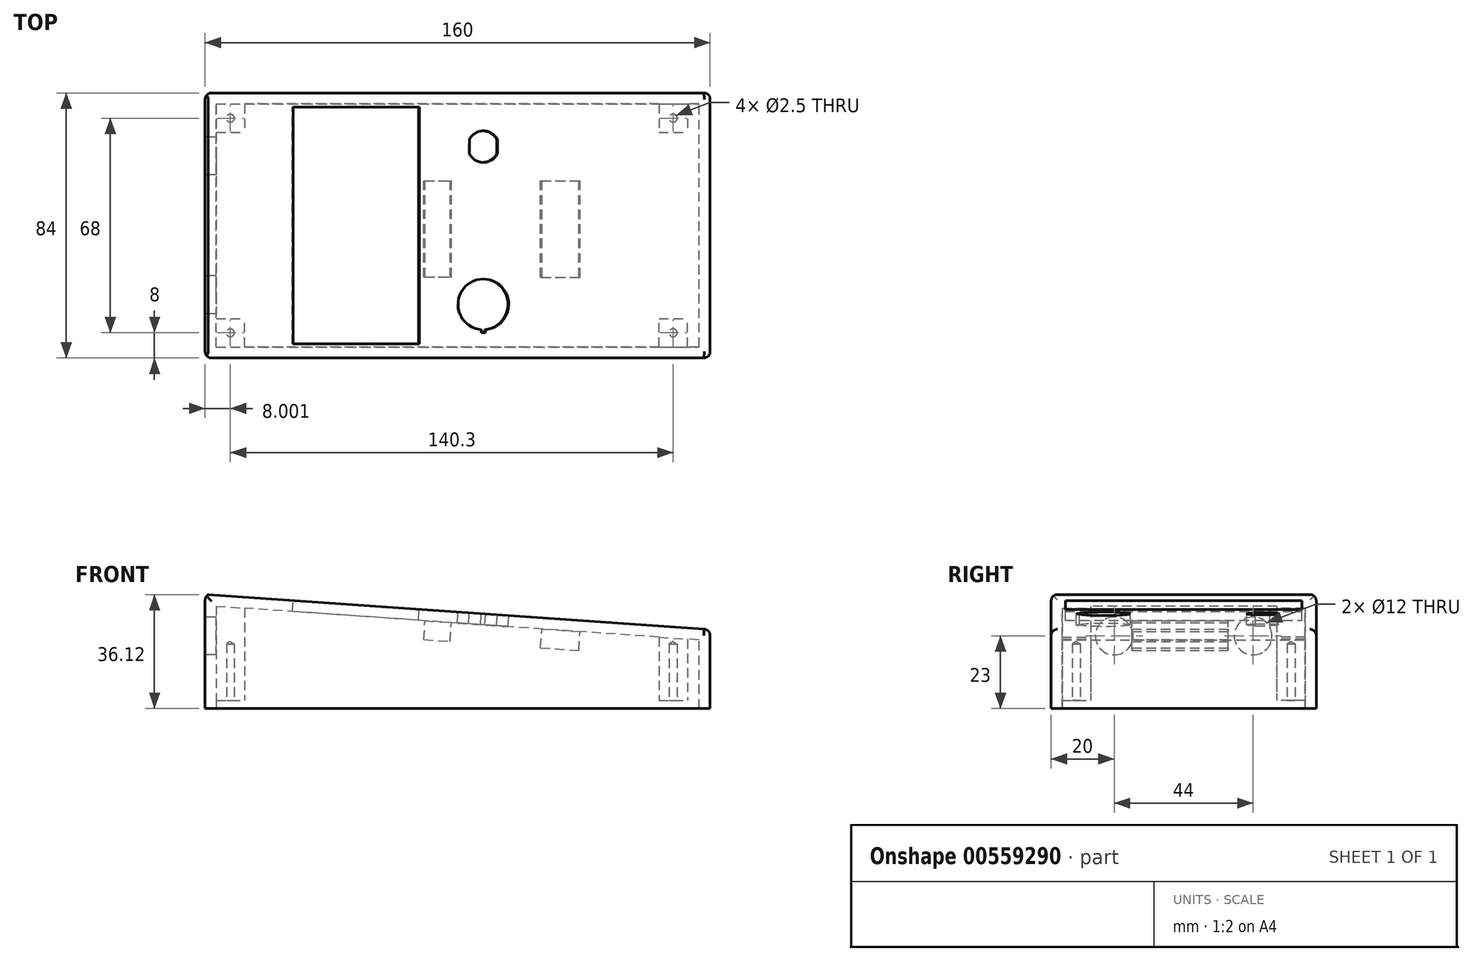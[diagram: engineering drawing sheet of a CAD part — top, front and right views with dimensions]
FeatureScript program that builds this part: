
annotation { "Feature Type Name" : "Feature", "Feature Type Description" : "" }
export const myFeature = defineFeature(function(context is Context, id is Id, definition is map)
    precondition{}
    {
        {
            var Q0;
            Q0=qCreatedBy(makeId("Front.planeOp"),FACE);
            var sketch = newSketch(context, id + "F0", { "sketchPlane" : qUnion([Q0])});
            skLineSegment(sketch, "E0", {"start": v(-94.59, 0) * mm, "end": v(103.68, 0) * mm, "construction": true});
            skLineSegment(sketch, "E1", {"start": v(0, 82.66) * mm, "end": v(0, -62.2) * mm, "construction": true});
            skLineSegment(sketch, "E2", {"start": v(-66.64, 0) * mm, "end": v(93.36, 0) * mm});
            skLineSegment(sketch, "E3", {"start": v(93.36, 0) * mm, "end": v(93.36, 25) * mm});
            skLineSegment(sketch, "E4", {"start": v(93.36, 25) * mm, "end": v(-65.64, 36.12) * mm});
            skLineSegment(sketch, "E5", {"start": v(-65.64, 36.12) * mm, "end": v(-66.64, 36.12) * mm});
            skLineSegment(sketch, "E6", {"start": v(-66.64, 36.12) * mm, "end": v(-66.64, 0) * mm});
            skLineSegment(sketch, "E7", {"start": v(93.36, 25) * mm, "end": v(-44.16, 25) * mm, "construction": true});
            skSolve(sketch);
        }
        {
            var Q0;
            Q0 = qSketchRegion(id + "F0", true);
            extrude(context, id + "F1", {"entities" : qUnion([Q0]), "endBound" : BoundingType.SYMMETRIC, "depth" : 84 * mm, "offsetDistance" : 25 * mm});
        }
        {
            var Q0;
            Q0=makeQuery(id+"F1.opExtrude","SWEPT_FACE",FACE,{"disambiguationData":[OSD([sQuery(id+"F0.wireOp",EDGE,"E2")])]});
            shell(context, id + "F2", {"entities" : qUnion([Q0]), "thickness" : 3.5 * mm});
        }
        {
            var Q0;
            Q0=makeQuery(id+"F1.opExtrude","SWEPT_FACE",FACE,{"disambiguationData":[OSD([sQuery(id+"F0.wireOp",EDGE,"E4")])]});
            var sketch = newSketch(context, id + "F3", { "sketchPlane" : qUnion([Q0])});
            skLineSegment(sketch, "E8", {"start": v(-77.74, 0) * mm, "end": v(107.26, 0) * mm, "construction": true});
            skLineSegment(sketch, "E9", {"start": v(-2.68, 70.27) * mm, "end": v(-2.68, -46.47) * mm, "construction": true});
            skLineSegment(sketch, "E10", {"start": v(31.39, 67.05) * mm, "end": v(31.39, -68) * mm, "construction": true});
            skLineSegment(sketch, "E11", {"start": v(19.39, -65.22) * mm, "end": v(19.39, 69.42) * mm, "construction": true});
            skLineSegment(sketch, "E12", {"start": v(9.3, -25) * mm, "end": v(38.07, -25) * mm, "construction": true});
            skLineSegment(sketch, "E13", {"start": v(15.02, 25) * mm, "end": v(38.07, 25) * mm, "construction": true});
            skLineSegment(sketch, "E14", {"start": v(-68, 65.02) * mm, "end": v(-68, -30.89) * mm, "construction": true});
            skLineSegment(sketch, "E15", {"start": v(-41, 65.02) * mm, "end": v(-41, -30.89) * mm, "construction": true});
            skLineSegment(sketch, "E16", {"start": v(-41, -30.89) * mm, "end": v(-42.3, -30.89) * mm, "construction": true});
            skLineSegment(sketch, "E17.bottom", {"start": v(-41, 37.5) * mm, "end": v(-1, 37.5) * mm});
            skLineSegment(sketch, "E17.top", {"start": v(-41, -37.5) * mm, "end": v(-1, -37.5) * mm});
            skLineSegment(sketch, "E17.left", {"start": v(-41, 37.5) * mm, "end": v(-41, -37.5) * mm});
            skLineSegment(sketch, "E17.right", {"start": v(-1, 37.5) * mm, "end": v(-1, -37.5) * mm});
            skLineSegment(sketch, "E18.MirrorCS", {"start": v(27.6, -25) * mm, "end": v(-1.18, -25) * mm, "construction": true});
            skArc(sketch, "E19", {"start": v(14.94, 22.72) * mm, "mid": v(19.39, 20) * mm, "end": v(23.84, 22.72) * mm});
            skLineSegment(sketch, "E20", {"start": v(14.94, 27.28) * mm, "end": v(14.94, 22.72) * mm});
            skLineSegment(sketch, "E21.MirrorCS", {"start": v(23.84, 27.28) * mm, "end": v(23.84, 22.72) * mm});
            skArc(sketch, "E22.trimOffspring", {"start": v(23.84, 27.28) * mm, "mid": v(19.39, 30) * mm, "end": v(14.94, 27.28) * mm});
            skArc(sketch, "E23", {"start": v(20.04, -33.02) * mm, "mid": v(19.39, -16.95) * mm, "end": v(18.74, -33.02) * mm});
            skLineSegment(sketch, "E24.top", {"start": v(18.74, -34.02) * mm, "end": v(20.04, -34.02) * mm});
            skLineSegment(sketch, "E24.left", {"start": v(18.74, -33.02) * mm, "end": v(18.74, -34.02) * mm});
            skLineSegment(sketch, "E24.right", {"start": v(20.04, -33.02) * mm, "end": v(20.04, -34.02) * mm});
            skSolve(sketch);
        }
        {
            var Q0;
            Q0=makeQuery(id+"F3.imprint","IMPRINT",FACE,{"disambiguationData":[TD([[makeQuery(id+"F3.imprint","IMPRINT",EDGE,{"derivedFrom":sQuery(id+"F3.wireOp",EDGE,"1abdff49-32a7-4e46-9834-f7d7c9bdcb830.MirrorCS")}),-1.0]])]});
            var Q1;
            Q1=makeQuery(id+"F3.imprint","IMPRINT",FACE,{"disambiguationData":[TD([[makeQuery(id+"F3.imprint","IMPRINT",EDGE,{"derivedFrom":sQuery(id+"F3.wireOp",EDGE,"Tb5Z7JnE-D9wR-4kkP-e9h7-nN8Eiio6d8Eo")}),1.0]])]});
            var Q2;
            Q2=makeQuery(id+"F3.imprint","IMPRINT",FACE,{"disambiguationData":[TD([[makeQuery(id+"F3.imprint","IMPRINT",EDGE,{"derivedFrom":sQuery(id+"F3.wireOp",EDGE,"E17.bottom")}),-1.0]])]});
            extrude(context, id + "F4", {"entities" : qUnion([Q0, Q1, Q2]), "operationType" : NewBodyOperationType.REMOVE, "oppositeDirection" : true, "depth" : 4 * mm, "offsetDistance" : 25 * mm});
        }
        {
            var Q0;
            Q0=makeQuery(id+"F1.opExtrude","SWEPT_FACE",FACE,{"disambiguationData":[OSD([sQuery(id+"F0.wireOp",EDGE,"E2")])]});
            cPlane(context, id + "F5", {"entities" : qUnion([Q0]), "cplaneType" : CPlaneType.OFFSET, "offset" : 0 * mm, "width" : 150 * mm, "height" : 150 * mm});
        }
        {
            var Q0;
            Q0=makeQuery(id+"F3.imprint","IMPRINT",FACE,{"disambiguationData":[TD([[makeQuery(id+"F3.imprint","IMPRINT",EDGE,{"derivedFrom":sQuery(id+"F3.wireOp",EDGE,"E19")}),1.0]])]});
            var Q1;
            Q1=makeQuery(id+"F3.imprint","IMPRINT",FACE,{"disambiguationData":[TD([[makeQuery(id+"F3.imprint","IMPRINT",EDGE,{"derivedFrom":sQuery(id+"F3.wireOp",EDGE,"E23")}),1.0]])]});
            extrude(context, id + "F6", {"entities" : qUnion([Q0, Q1]), "operationType" : NewBodyOperationType.REMOVE, "oppositeDirection" : true, "depth" : 5 * mm, "offsetDistance" : 25 * mm});
        }
        {
            var Q0;
            Q0=qCreatedBy(id+"F5.planeOp",FACE);
            cPlane(context, id + "F7", {"entities" : qUnion([Q0]), "cplaneType" : CPlaneType.OFFSET, "offset" : 2.5 * mm, "oppositeDirection" : true, "width" : 150 * mm, "height" : 150 * mm});
        }
        {
            var Q0;
            Q0=qCreatedBy(id+"F7.planeOp",FACE);
            var sketch = newSketch(context, id + "F8", { "sketchPlane" : qUnion([Q0])});
            skLineSegment(sketch, "E25", {"start": v(-103.66, 0) * mm, "end": v(127.76, 0) * mm, "construction": true});
            skLineSegment(sketch, "E26", {"start": v(0, 82.93) * mm, "end": v(0, -76.71) * mm, "construction": true});
            skLineSegment(sketch, "E27.bottom", {"start": v(-63.14, 38.5) * mm, "end": v(-54.14, 38.5) * mm});
            skLineSegment(sketch, "E27.top", {"start": v(-63.14, 29.5) * mm, "end": v(-54.14, 29.5) * mm});
            skLineSegment(sketch, "E27.left", {"start": v(-63.14, 38.5) * mm, "end": v(-63.14, 29.5) * mm});
            skLineSegment(sketch, "E27.right", {"start": v(-54.14, 38.5) * mm, "end": v(-54.14, 29.5) * mm});
            skLineSegment(sketch, "E28.bottom", {"start": v(77.16, 38.5) * mm, "end": v(86.16, 38.5) * mm});
            skLineSegment(sketch, "E28.top", {"start": v(77.16, 29.5) * mm, "end": v(86.16, 29.5) * mm});
            skLineSegment(sketch, "E28.left", {"start": v(77.16, 38.5) * mm, "end": v(77.16, 29.5) * mm});
            skLineSegment(sketch, "E28.right", {"start": v(86.16, 38.5) * mm, "end": v(86.16, 29.5) * mm});
            skLineSegment(sketch, "E29.MirrorCS", {"start": v(-63.14, -29.5) * mm, "end": v(-54.14, -29.5) * mm});
            skLineSegment(sketch, "E30.MirrorCS", {"start": v(-63.14, -38.5) * mm, "end": v(-54.14, -38.5) * mm});
            skLineSegment(sketch, "E31.MirrorCS", {"start": v(-63.14, -38.5) * mm, "end": v(-63.14, -29.5) * mm});
            skLineSegment(sketch, "E32.MirrorCS", {"start": v(-54.14, -38.5) * mm, "end": v(-54.14, -29.5) * mm});
            skLineSegment(sketch, "E33.MirrorCS", {"start": v(77.16, -38.5) * mm, "end": v(77.16, -29.5) * mm});
            skLineSegment(sketch, "E34.MirrorCS", {"start": v(77.16, -38.5) * mm, "end": v(86.16, -38.5) * mm});
            skLineSegment(sketch, "E35.MirrorCS", {"start": v(86.16, -38.5) * mm, "end": v(86.16, -29.5) * mm});
            skLineSegment(sketch, "E36.MirrorCS", {"start": v(77.16, -29.5) * mm, "end": v(86.16, -29.5) * mm});
            skLineSegment(sketch, "E37", {"start": v(-58.64, 39.07) * mm, "end": v(-58.64, 26.98) * mm, "construction": true});
            skLineSegment(sketch, "E38", {"start": v(-63.59, 34) * mm, "end": v(-52.8, 34) * mm, "construction": true});
            skPoint(sketch, "E38.startSnap0", {"position": v(-63.14, 34) * mm});
            skPoint(sketch, "E39", {"position": v(-58.64, 34) * mm});
            skPoint(sketch, "E40.MirrorP", {"position": v(-58.64, -34) * mm});
            skLineSegment(sketch, "E41", {"start": v(70.14, 34) * mm, "end": v(88.02, 34) * mm, "construction": true});
            skLineSegment(sketch, "E42", {"start": v(81.66, 26.58) * mm, "end": v(81.66, 42.04) * mm, "construction": true});
            skPoint(sketch, "E43", {"position": v(81.66, 34) * mm});
            skPoint(sketch, "E44.MirrorP", {"position": v(81.66, -34) * mm});
            skSolve(sketch);
        }
        {
            var Q0;
            Q0=makeQuery(id+"F8.imprint","IMPRINT",FACE,{"disambiguationData":[TD([[makeQuery(id+"F8.imprint","IMPRINT",EDGE,{"derivedFrom":sQuery(id+"F8.wireOp",EDGE,"E28.bottom")}),-1.0]])]});
            var Q1;
            Q1=makeQuery(id+"F8.imprint","IMPRINT",FACE,{"disambiguationData":[TD([[makeQuery(id+"F8.imprint","IMPRINT",EDGE,{"derivedFrom":sQuery(id+"F8.wireOp",EDGE,"E33.MirrorCS")}),-1.0]])]});
            extrude(context, id + "F9", {"entities" : qUnion([Q0, Q1]), "operationType" : NewBodyOperationType.ADD, "oppositeDirection" : true, "depth" : 20.5 * mm, "offsetDistance" : 25 * mm});
        }
        {
            var Q0;
            Q0=makeQuery(id+"F8.imprint","IMPRINT",FACE,{"disambiguationData":[TD([[makeQuery(id+"F8.imprint","IMPRINT",EDGE,{"derivedFrom":sQuery(id+"F8.wireOp",EDGE,"E29.MirrorCS")}),-1.0]])]});
            var Q1;
            Q1=makeQuery(id+"F8.imprint","IMPRINT",FACE,{"disambiguationData":[TD([[makeQuery(id+"F8.imprint","IMPRINT",EDGE,{"derivedFrom":sQuery(id+"F8.wireOp",EDGE,"E27.bottom")}),-1.0]])]});
            extrude(context, id + "F10", {"entities" : qUnion([Q0, Q1]), "operationType" : NewBodyOperationType.ADD, "oppositeDirection" : true, "depth" : 32 * mm, "offsetDistance" : 25 * mm});
        }
        {
            var Q0;
            Q0=makeQuery(id+"F1.opExtrude","SWEPT_FACE",FACE,{"disambiguationData":[OSD([sQuery(id+"F0.wireOp",EDGE,"E6")])]});
            cPlane(context, id + "F11", {"entities" : qUnion([Q0]), "cplaneType" : CPlaneType.OFFSET, "offset" : 0 * mm, "width" : 150 * mm, "height" : 150 * mm});
        }
        {
            var Q0;
            Q0=qCreatedBy(id+"F11.planeOp",FACE);
            var sketch = newSketch(context, id + "F12", { "sketchPlane" : qUnion([Q0])});
            skLineSegment(sketch, "E45", {"start": v(0, 66.56) * mm, "end": v(0, -24.94) * mm, "construction": true});
            skLineSegment(sketch, "E46", {"start": v(-59.79, 38) * mm, "end": v(68.65, 38) * mm, "construction": true});
            skLineSegment(sketch, "E47", {"start": v(-22, 58.02) * mm, "end": v(-22, -9.78) * mm, "construction": true});
            skLineSegment(sketch, "E48", {"start": v(-40, 53.44) * mm, "end": v(-40, -9.78) * mm, "construction": true});
            skLineSegment(sketch, "E49", {"start": v(-40, -9.78) * mm, "end": v(-39.37, -8.84) * mm, "construction": true});
            skLineSegment(sketch, "E50", {"start": v(-68.53, 23) * mm, "end": v(71, 23) * mm, "construction": true});
            skCircle(sketch, "E51", {"center": v(-22, 23) * mm, "radius": 6 * mm});
            skPoint(sketch, "E51.centerSnap0", {"position": v(-22, 24.12) * mm});
            skCircle(sketch, "E52.MirrorC", {"center": v(22, 23) * mm, "radius": 6 * mm});
            skSolve(sketch);
        }
        {
            var Q0;
            Q0 = qSketchRegion(id + "F12", true);
            extrude(context, id + "F13", {"entities" : qUnion([Q0]), "operationType" : NewBodyOperationType.REMOVE, "oppositeDirection" : true, "depth" : 25 * mm, "offsetDistance" : 25 * mm});
        }
        {
            var Q0;
            Q0=makeQuery(id+"F2.opShell","OFFSET_FACE",FACE,{"disambiguationData":[OSD([sQuery(id+"F0.wireOp",EDGE,"E4")])]});
            var Q1;
            Q1 = qBodyType(qCreatedBy(id + "F15" ,EDGE), BodyType.WIRE);
            cPlane(context, id + "F14", {"entities" : qUnion([Q0, Q1]), "cplaneType" : CPlaneType.OFFSET, "offset" : 0 * mm, "width" : 150 * mm, "height" : 150 * mm});
        }
        {
            var Q0;
            Q0=qCreatedBy(id+"F14.planeOp",FACE);
            var sketch = newSketch(context, id + "F15", { "sketchPlane" : qUnion([Q0])});
            skLineSegment(sketch, "E53.bottom", {"start": v(1.11, 16.35) * mm, "end": v(9.47, 16.35) * mm});
            skLineSegment(sketch, "E53.top", {"start": v(1.11, -14.11) * mm, "end": v(9.47, -14.11) * mm});
            skLineSegment(sketch, "E53.left", {"start": v(1.11, 16.35) * mm, "end": v(1.11, -14.11) * mm});
            skLineSegment(sketch, "E53.right", {"start": v(9.47, 16.35) * mm, "end": v(9.47, -14.11) * mm});
            skLineSegment(sketch, "E54.bottom", {"start": v(38.2, 16.39) * mm, "end": v(50.35, 16.39) * mm});
            skLineSegment(sketch, "E54.top", {"start": v(38.2, -14.12) * mm, "end": v(50.35, -14.12) * mm});
            skLineSegment(sketch, "E54.left", {"start": v(38.2, 16.39) * mm, "end": v(38.2, -14.12) * mm});
            skLineSegment(sketch, "E54.right", {"start": v(50.35, 16.39) * mm, "end": v(50.35, -14.12) * mm});
            skLineSegment(sketch, "E55", {"start": v(1.82, 16.35) * mm, "end": v(46.73, 16.35) * mm, "construction": true});
            skLineSegment(sketch, "E56", {"start": v(6.13, -14.11) * mm, "end": v(47.72, -14.11) * mm, "construction": true});
            skSolve(sketch);
        }
        {
            var Q0;
            Q0=makeQuery(id+"F15.imprint","IMPRINT",FACE,{"disambiguationData":[TD([[makeQuery(id+"F15.imprint","IMPRINT",EDGE,{"derivedFrom":sQuery(id+"F15.wireOp",EDGE,"E53.bottom")}),-1.0]])]});
            var Q1;
            Q1=makeQuery(id+"F15.imprint","IMPRINT",FACE,{"disambiguationData":[TD([[makeQuery(id+"F15.imprint","IMPRINT",EDGE,{"derivedFrom":sQuery(id+"F15.wireOp",EDGE,"E54.bottom")}),-1.0]])]});
            extrude(context, id + "F16", {"entities" : qUnion([Q0, Q1]), "operationType" : NewBodyOperationType.ADD, "depth" : 6 * mm, "offsetDistance" : 25 * mm});
        }
        {
            var Q0;
            Q0=makeQuery(id+"F1.opExtrude","CAP_EDGE",EDGE,{"disambiguationData":[OSD([sQuery(id+"F0.wireOp",EDGE,"E4")])],"isStart":true});
            var Q1;
            Q1=makeQuery(id+"F1.opExtrude","SWEPT_EDGE",EDGE,{"disambiguationData":[OSD([sQuery(id+"F0.wireOp",EDGE,"E5"),sQuery(id+"F0.wireOp",EDGE,"E6")])]});
            var Q2;
            Q2=makeQuery(id+"F1.opExtrude","CAP_EDGE",EDGE,{"disambiguationData":[OSD([sQuery(id+"F0.wireOp",EDGE,"E6")])],"isStart":true});
            var Q3;
            Q3=makeQuery(id+"F1.opExtrude","CAP_EDGE",EDGE,{"disambiguationData":[OSD([sQuery(id+"F0.wireOp",EDGE,"E6")])],"isStart":false});
            var Q4;
            Q4=makeQuery(id+"F1.opExtrude","CAP_EDGE",EDGE,{"disambiguationData":[OSD([sQuery(id+"F0.wireOp",EDGE,"E4")])],"isStart":false});
            var Q5;
            Q5=makeQuery(id+"F1.opExtrude","CAP_EDGE",EDGE,{"disambiguationData":[OSD([sQuery(id+"F0.wireOp",EDGE,"E3")])],"isStart":true});
            var Q6;
            Q6=makeQuery(id+"F1.opExtrude","CAP_EDGE",EDGE,{"disambiguationData":[OSD([sQuery(id+"F0.wireOp",EDGE,"E3")])],"isStart":false});
            fillet(context, id + "F17", {"entities" : qUnion([Q0, Q1, Q2, Q3, Q4, Q5, Q6]), "radius" : 2 * mm, "tangentPropagation" : true, "allowEdgeOverflow" : false});
        }
        {
            var Q0;
            Q0=sQuery(id+"F8.wireOp",VERTEX,"E39");
            var Q1;
            Q1=sQuery(id+"F8.wireOp",VERTEX,"E40.MirrorP");
            var Q2;
            Q2=makeQuery(id+"F1.opExtrude","SWEPT_BODY",BODY,{"disambiguationData":[OSD([sQuery(id+"F0.wireOp",EDGE,"E2"),sQuery(id+"F0.wireOp",EDGE,"E3"),sQuery(id+"F0.wireOp",EDGE,"E4"),sQuery(id+"F0.wireOp",EDGE,"E5"),sQuery(id+"F0.wireOp",EDGE,"E6")])]});
            hole(context, id + "F18", {"style" : HoleStyle.SIMPLE, "endStyle" : HoleEndStyle.BLIND, "standardTappedOrClearance" : lookupTablePath({ "standard" : "ISO", "size" : "2.5", "type" : "Drilled" }), "standardBlindInLast" : lookupTablePath({ "standard" : "ISO", "size" : "2.5", "type" : "Drilled" }), "holeDiameter" : 2.5 * mm, "majorDiameter" : 5 * mm, "holeDepth" : 18 * mm, "isTappedThrough" : true, "tappedDepth" : 12 * mm, "tapClearance" : 3, "startFromSketch" : true, "locations" : qUnion([Q0, Q1]), "scope" : qUnion([Q2])});
        }
        {
            var Q0;
            Q0=makeQuery(id+"F1.opExtrude","SWEPT_EDGE",EDGE,{"disambiguationData":[OSD([sQuery(id+"F0.wireOp",EDGE,"E3"),sQuery(id+"F0.wireOp",EDGE,"E4")])]});
            fillet(context, id + "F19", {"entities" : qUnion([Q0]), "radius" : 2 * mm, "tangentPropagation" : true, "allowEdgeOverflow" : false});
        }
        {
            var Q0;
            Q0=sQuery(id+"F8.wireOp",VERTEX,"E43");
            var Q1;
            Q1=sQuery(id+"F8.wireOp",VERTEX,"E44.MirrorP");
            var Q2;
            Q2=makeQuery(id+"F1.opExtrude","SWEPT_BODY",BODY,{"disambiguationData":[OSD([sQuery(id+"F0.wireOp",EDGE,"E2"),sQuery(id+"F0.wireOp",EDGE,"E3"),sQuery(id+"F0.wireOp",EDGE,"E4"),sQuery(id+"F0.wireOp",EDGE,"E5"),sQuery(id+"F0.wireOp",EDGE,"E6")])]});
            hole(context, id + "F20", {"style" : HoleStyle.SIMPLE, "endStyle" : HoleEndStyle.BLIND, "standardTappedOrClearance" : lookupTablePath({ "standard" : "ISO", "size" : "2.5", "type" : "Drilled" }), "standardBlindInLast" : lookupTablePath({ "standard" : "ISO", "size" : "2.5", "type" : "Drilled" }), "holeDiameter" : 2.5 * mm, "majorDiameter" : 5 * mm, "holeDepth" : 18 * mm, "isTappedThrough" : true, "tappedDepth" : 12 * mm, "tapClearance" : 3, "startFromSketch" : true, "locations" : qUnion([Q0, Q1]), "scope" : qUnion([Q2])});
        }
    });
